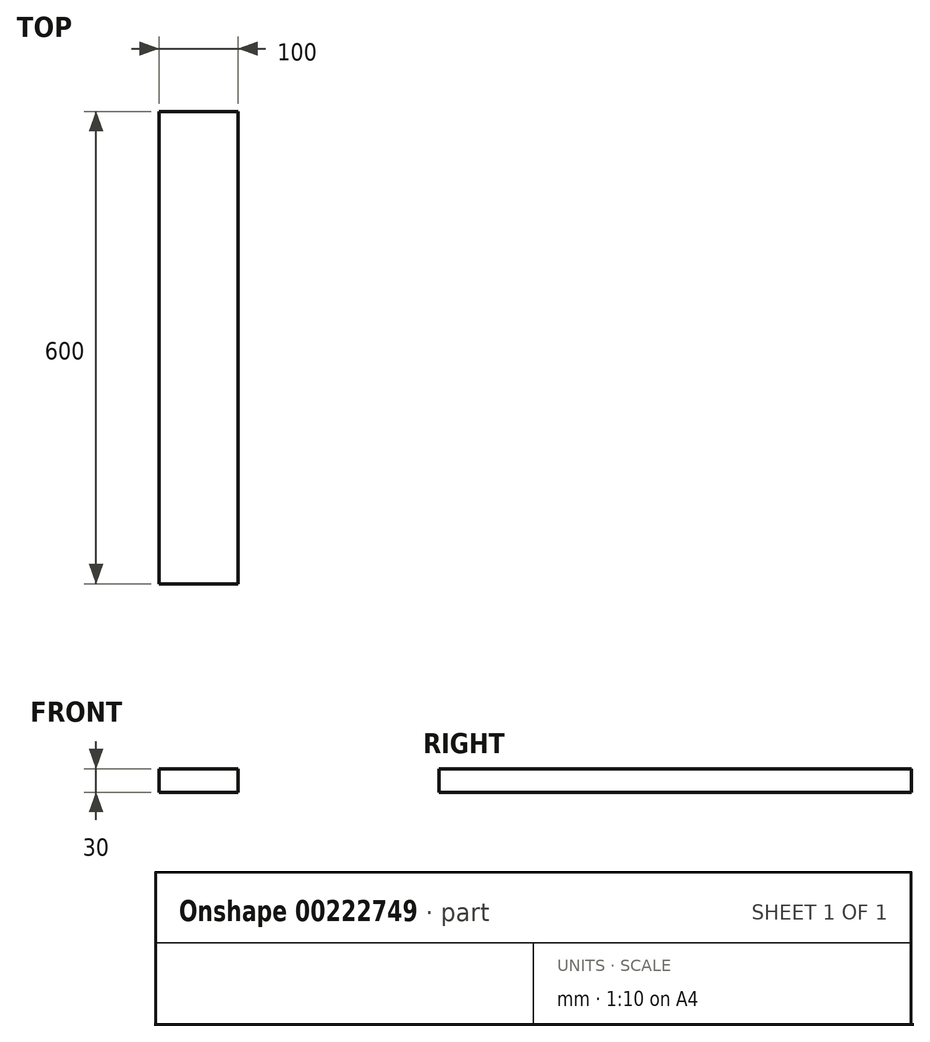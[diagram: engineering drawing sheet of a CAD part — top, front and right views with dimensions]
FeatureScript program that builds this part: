
annotation { "Feature Type Name" : "Feature", "Feature Type Description" : "" }
export const myFeature = defineFeature(function(context is Context, id is Id, definition is map)
    precondition{}
    {
        {
            var Q0;
            Q0=qCreatedBy(makeId("Top.planeOp"),FACE);
            var sketch = newSketch(context, id + "F0", { "sketchPlane" : qUnion([Q0])});
            skLineSegment(sketch, "E0.bottom", {"start": v(32.5, -100.2) * mm, "end": v(-67.5, -100.2) * mm});
            skLineSegment(sketch, "E0.top", {"start": v(32.5, -700.2) * mm, "end": v(-67.5, -700.2) * mm});
            skLineSegment(sketch, "E0.left", {"start": v(32.5, -100.2) * mm, "end": v(32.5, -700.2) * mm});
            skLineSegment(sketch, "E0.right", {"start": v(-67.5, -100.2) * mm, "end": v(-67.5, -700.2) * mm});
            skPoint(sketch, "E0.middle", {"position": v(-17.5, -400.2) * mm});
            skSolve(sketch);
        }
        {
            var Q0;
            Q0 = qSketchRegion(id + "F0", true);
            extrude(context, id + "F1", {"entities" : qUnion([Q0]), "depth" : 30 * mm});
        }
    });
